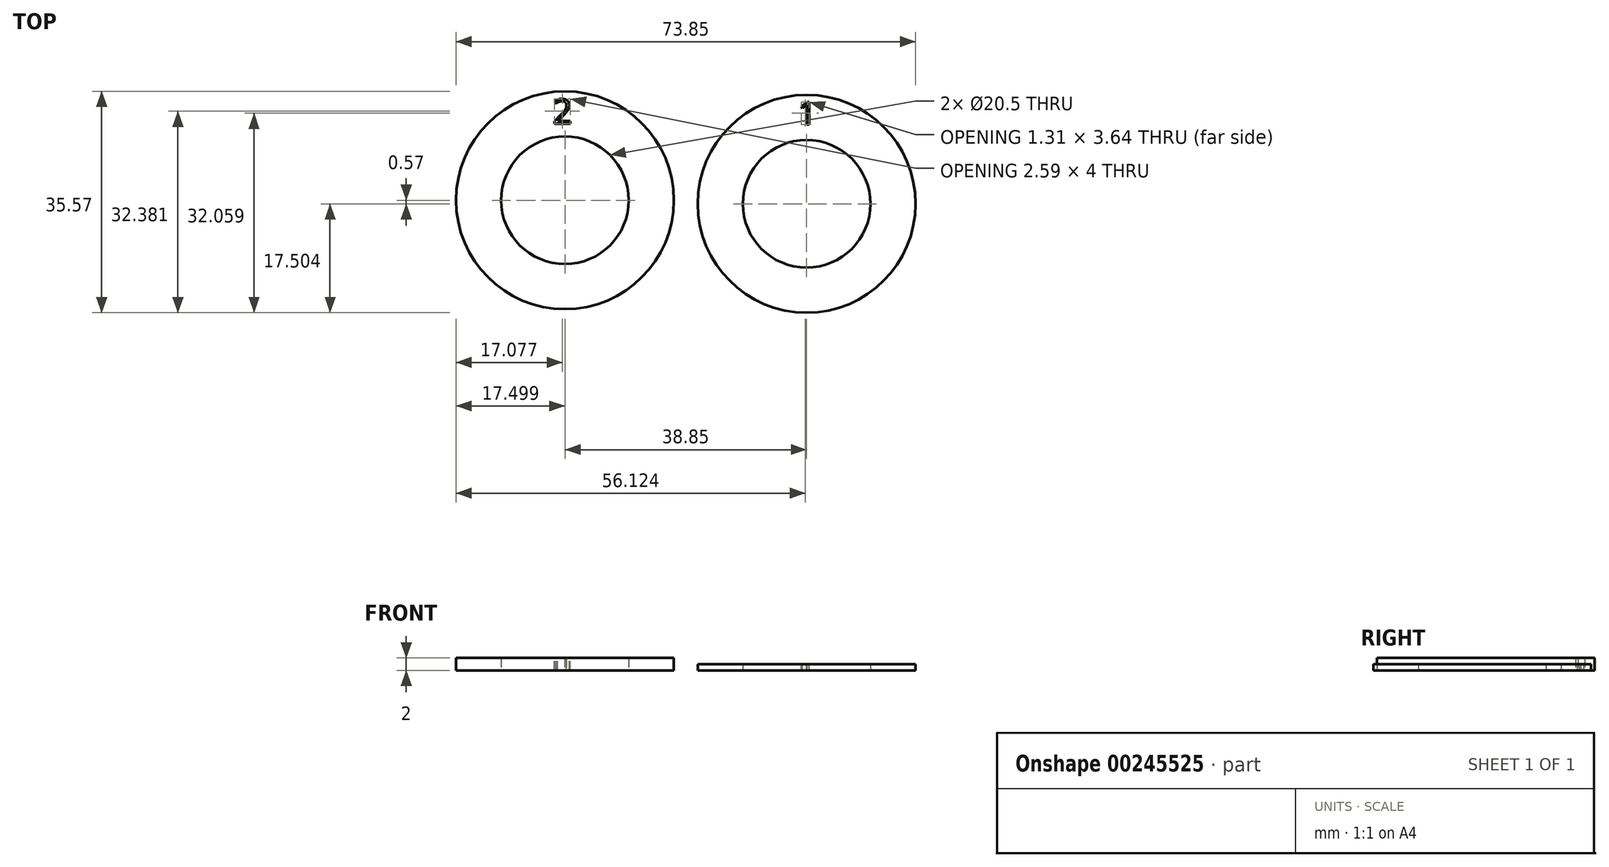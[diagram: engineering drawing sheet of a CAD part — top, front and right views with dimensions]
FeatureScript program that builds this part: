
annotation { "Feature Type Name" : "Feature", "Feature Type Description" : "" }
export const myFeature = defineFeature(function(context is Context, id is Id, definition is map)
    precondition{}
    {
        {
            var Q0;
            Q0=qCreatedBy(makeId("Top.planeOp"),FACE);
            var sketch = newSketch(context, id + "F0", { "sketchPlane" : qUnion([Q0])});
            skCircle(sketch, "E0", {"center": v(-32.96, 29.34) * mm, "radius": 10.25 * mm});
            skCircle(sketch, "E1", {"center": v(-32.96, 29.34) * mm, "radius": 17.5 * mm});
            skSolve(sketch);
        }
        {
            var Q0;
            Q0=makeQuery(id+"F0.imprint","IMPRINT",FACE,{"disambiguationData":[TD([[makeQuery(id+"F0.imprint","IMPRINT",EDGE,{"derivedFrom":sQuery(id+"F0.wireOp",EDGE,"E0")}),-1.0]])]});
            extrude(context, id + "F1", {"entities" : qUnion([Q0]), "depth" : 2 * mm});
        }
        {
            var Q0;
            Q0=makeQuery(id+"F1.opExtrude","CAP_FACE",FACE,{"disambiguationData":[OSD([sQuery(id+"F0.wireOp",EDGE,"E0"),sQuery(id+"F0.wireOp",EDGE,"E1")])],"isStart":false});
            var sketch = newSketch(context, id + "F2", { "sketchPlane" : qUnion([Q0])});
            skText(sketch, "E2", { "text": "2", "fontName": "OpenSans-Regular.ttf"});
            const initialGuessF2  = {"E2": [-0.03495, 0.04165, 1, 0, 0.00398]};
            skSetInitialGuess(sketch, initialGuessF2);
            skSolve(sketch);
        }
        {
            var Q0;
            Q0 = qSketchRegion(id + "F2", true);
            extrude(context, id + "F3", {"entities" : qUnion([Q0]), "operationType" : NewBodyOperationType.REMOVE, "oppositeDirection" : true, "depth" : 2 * mm});
        }
        {
            var Q0;
            Q0=qCreatedBy(makeId("Top.planeOp"),FACE);
            var sketch = newSketch(context, id + "F4", { "sketchPlane" : qUnion([Q0])});
            skCircle(sketch, "E3", {"center": v(5.89, 28.77) * mm, "radius": 17.5 * mm});
            skCircle(sketch, "E4", {"center": v(5.89, 28.77) * mm, "radius": 10.25 * mm});
            skSolve(sketch);
        }
        {
            var Q0;
            Q0=makeQuery(id+"F4.imprint","IMPRINT",FACE,{"disambiguationData":[TD([[makeQuery(id+"F4.imprint","IMPRINT",EDGE,{"derivedFrom":sQuery(id+"F4.wireOp",EDGE,"E3")}),1.0]])]});
            extrude(context, id + "F5", {"entities" : qUnion([Q0]), "depth" : 1 * mm});
        }
        {
            var Q0;
            Q0=makeQuery(id+"F5.opExtrude","CAP_FACE",FACE,{"disambiguationData":[OSD([sQuery(id+"F4.wireOp",EDGE,"E3"),sQuery(id+"F4.wireOp",EDGE,"E4")])],"isStart":false});
            var sketch = newSketch(context, id + "F6", { "sketchPlane" : qUnion([Q0])});
            skText(sketch, "E5", { "text": "1", "fontName": "OpenSans-Regular.ttf"});
            const initialGuessF6  = {"E5": [0.00454, 0.04151, 1, 0, 0.00367]};
            skSetInitialGuess(sketch, initialGuessF6);
            skSolve(sketch);
        }
        {
            var Q0;
            Q0 = qSketchRegion(id + "F6", true);
            extrude(context, id + "F7", {"entities" : qUnion([Q0]), "operationType" : NewBodyOperationType.REMOVE, "oppositeDirection" : true, "depth" : 1 * mm});
        }
    });
